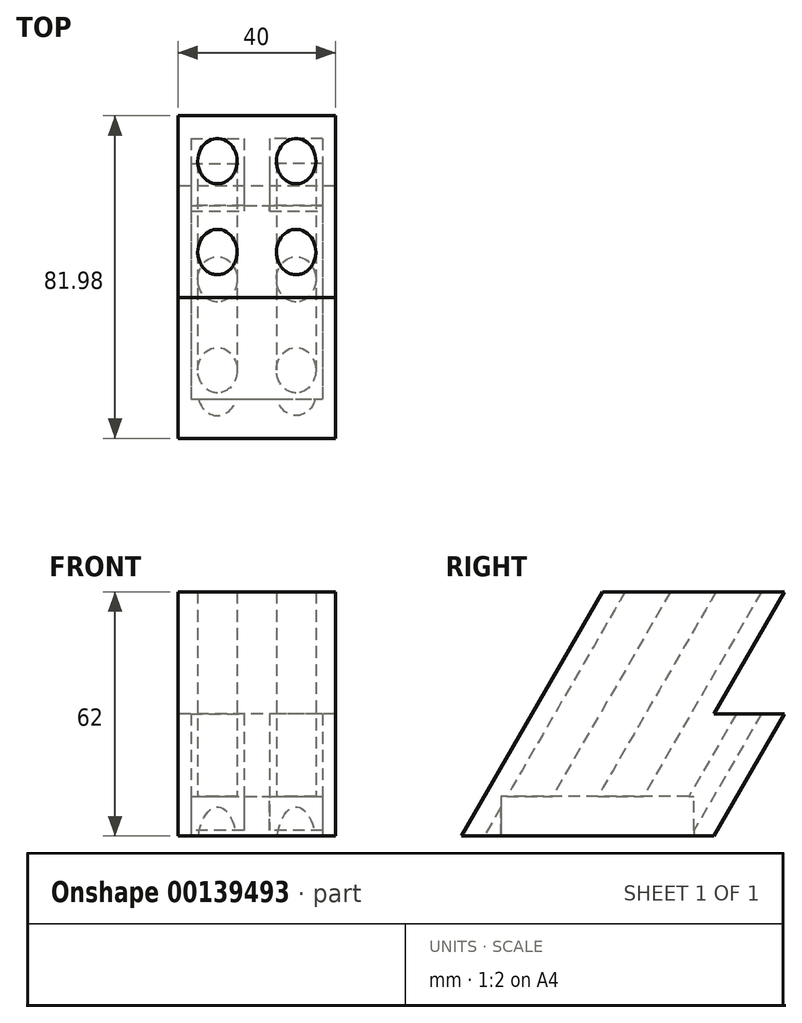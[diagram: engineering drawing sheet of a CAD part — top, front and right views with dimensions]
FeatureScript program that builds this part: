
annotation { "Feature Type Name" : "Feature", "Feature Type Description" : "" }
export const myFeature = defineFeature(function(context is Context, id is Id, definition is map)
    precondition{}
    {
        {
            var Q0;
            Q0=qCreatedBy(makeId("Right.planeOp"),FACE);
            var sketch = newSketch(context, id + "F0", { "sketchPlane" : qUnion([Q0])});
            skLineSegment(sketch, "E0", {"start": v(0, 0) * mm, "end": v(35.8, 62) * mm});
            skLineSegment(sketch, "E1", {"start": v(35.8, 62) * mm, "end": v(81.98, 62) * mm});
            skLineSegment(sketch, "E2", {"start": v(81.98, 62) * mm, "end": v(64.09, 31) * mm});
            skLineSegment(sketch, "E3", {"start": v(46.19, 0) * mm, "end": v(0, 0) * mm});
            skLineSegment(sketch, "E4", {"start": v(46.19, 0) * mm, "end": v(64.09, 0) * mm});
            skPoint(sketch, "E4.endSnap0", {"position": v(64.09, 31) * mm});
            skLineSegment(sketch, "E5", {"start": v(64.09, 0) * mm, "end": v(81.98, 31) * mm});
            skLineSegment(sketch, "E6", {"start": v(81.98, 31) * mm, "end": v(64.09, 31) * mm});
            skLineSegment(sketch, "E7", {"start": v(64.09, 0) * mm, "end": v(16.02, 27.75) * mm, "construction": true});
            skLineSegment(sketch, "E8", {"start": v(64.09, 31) * mm, "end": v(29.44, 51) * mm, "construction": true});
            skSolve(sketch);
        }
        {
            var Q0;
            Q0 = qSketchRegion(id + "F0", true);
            extrude(context, id + "F1", {"entities" : qUnion([Q0]), "depth" : 20 * mm});
        }
        {
            var Q0;
            Q0=sQuery(id+"F0.wireOp",EDGE,"E7");
            cPlane(context, id + "F2", {"entities" : qUnion([Q0]), "cplaneType" : CPlaneType.LINE_ANGLE, "offset" : 25 * mm, "angle" : 0 * degree, "width" : 150 * mm, "height" : 150 * mm});
        }
        {
            var Q0;
            Q0=qCreatedBy(id+"F2.planeOp",FACE);
            var sketch = newSketch(context, id + "F3", { "sketchPlane" : qUnion([Q0])});
            skCircle(sketch, "E9", {"center": v(10, -10) * mm, "radius": 5 * mm});
            skCircle(sketch, "E10", {"center": v(10, -30) * mm, "radius": 5 * mm});
            skLineSegment(sketch, "E11.bottom", {"start": v(16.75, -50.5) * mm, "end": v(3.25, -50.5) * mm});
            skLineSegment(sketch, "E11.top", {"start": v(16.75, -45) * mm, "end": v(3.25, -45) * mm});
            skLineSegment(sketch, "E11.left", {"start": v(16.75, -50.5) * mm, "end": v(16.75, -45) * mm});
            skLineSegment(sketch, "E11.right", {"start": v(3.25, -50.5) * mm, "end": v(3.25, -45) * mm});
            skSolve(sketch);
        }
        {
            var Q0;
            Q0 = qSketchRegion(id + "F3", true);
            extrude(context, id + "F4", {"entities" : qUnion([Q0]), "operationType" : NewBodyOperationType.REMOVE, "endBound" : BoundingType.SYMMETRIC, "oppositeDirection" : true, "depth" : 1000 * mm});
        }
        {
            var Q0;
            Q0=makeQuery(id+"F1.opExtrude","SWEPT_BODY",BODY,{"disambiguationData":[OSD([sQuery(id+"F0.wireOp",EDGE,"E0"),sQuery(id+"F0.wireOp",EDGE,"E1"),sQuery(id+"F0.wireOp",EDGE,"E2"),sQuery(id+"F0.wireOp",EDGE,"E3"),sQuery(id+"F0.wireOp",EDGE,"E4"),sQuery(id+"F0.wireOp",EDGE,"E5"),sQuery(id+"F0.wireOp",EDGE,"E6")])]});
            var Q1;
            Q1=qCreatedBy(makeId("Right.planeOp"),FACE);
            mirror(context, id + "F5", {"operationType" : NewBodyOperationType.ADD, "entities" : qUnion([Q0]), "mirrorPlane" : qUnion([Q1])});
        }
        {
            var Q0;
            {var subQ0=makeQuery(id+"F1.opExtrude","SWEPT_FACE",FACE,{"disambiguationData":[OSD([sQuery(id+"F0.wireOp",EDGE,"E3"),sQuery(id+"F0.wireOp",EDGE,"E4")])]});Q0=makeQuery(id+"F5.boolean.opBoolean","MERGE",FACE,{"derivedFrom":[subQ0,makeQuery(id+"F5.opPattern","COPY",FACE,{"derivedFrom":subQ0,"instanceName":"1"})]});}
            var sketch = newSketch(context, id + "F6", { "sketchPlane" : qUnion([Q0])});
            skLineSegment(sketch, "E12.bottom", {"start": v(-16.75, -10) * mm, "end": v(16.75, -10) * mm});
            skLineSegment(sketch, "E12.top", {"start": v(-16.75, -59.09) * mm, "end": v(16.75, -59.09) * mm});
            skLineSegment(sketch, "E12.left", {"start": v(-16.75, -10) * mm, "end": v(-16.75, -59.09) * mm});
            skLineSegment(sketch, "E12.right", {"start": v(16.75, -10) * mm, "end": v(16.75, -59.09) * mm});
            skSolve(sketch);
        }
        {
            var Q0;
            Q0 = qSketchRegion(id + "F6", true);
            extrude(context, id + "F7", {"entities" : qUnion([Q0]), "operationType" : NewBodyOperationType.REMOVE, "oppositeDirection" : true, "depth" : 10 * mm});
        }
    });
